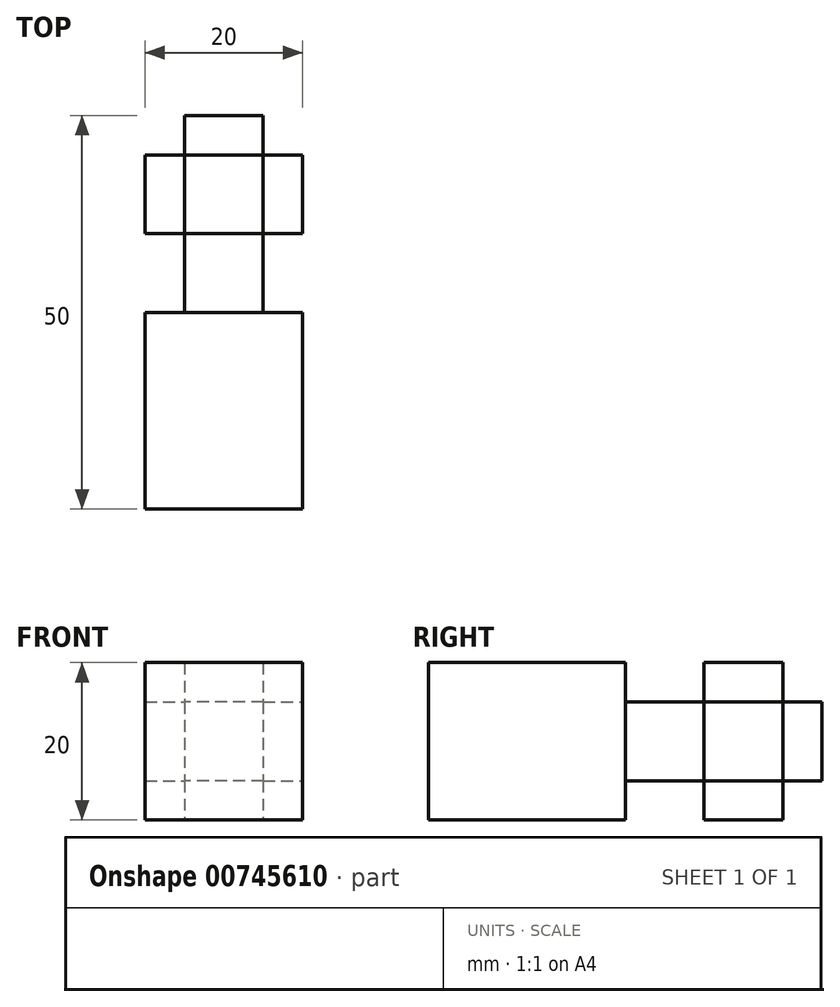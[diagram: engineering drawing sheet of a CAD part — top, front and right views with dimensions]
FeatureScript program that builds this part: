
annotation { "Feature Type Name" : "Feature", "Feature Type Description" : "" }
export const myFeature = defineFeature(function(context is Context, id is Id, definition is map)
    precondition{}
    {
        {
            var Q0;
            Q0=qCreatedBy(makeId("Front.planeOp"),FACE);
            var sketch = newSketch(context, id + "F0", { "sketchPlane" : qUnion([Q0])});
            skLineSegment(sketch, "E0.bottom", {"start": v(-5, 5) * mm, "end": v(5, 5) * mm});
            skLineSegment(sketch, "E0.top", {"start": v(-5, -5) * mm, "end": v(5, -5) * mm});
            skLineSegment(sketch, "E0.left", {"start": v(-5, 5) * mm, "end": v(-5, -5) * mm});
            skLineSegment(sketch, "E0.right", {"start": v(5, 5) * mm, "end": v(5, -5) * mm});
            skPoint(sketch, "E0.middle", {"position": v(0, 0) * mm});
            skSolve(sketch);
        }
        {
            var Q0;
            Q0 = qSketchRegion(id + "F0", true);
            extrude(context, id + "F1", {"entities" : qUnion([Q0]), "depth" : 25 * mm, "offsetDistance" : 25 * mm});
        }
        {
            var Q0;
            Q0=makeQuery(id+"F1.opExtrude","CAP_FACE",FACE,{"disambiguationData":[OSD([sQuery(id+"F0.wireOp",EDGE,"E0.bottom"),sQuery(id+"F0.wireOp",EDGE,"E0.top"),sQuery(id+"F0.wireOp",EDGE,"E0.left"),sQuery(id+"F0.wireOp",EDGE,"E0.right")])],"isStart":false});
            var sketch = newSketch(context, id + "F2", { "sketchPlane" : qUnion([Q0])});
            skLineSegment(sketch, "E1.bottom", {"start": v(-10, 10) * mm, "end": v(10, 10) * mm});
            skLineSegment(sketch, "E1.top", {"start": v(-10, -10) * mm, "end": v(10, -10) * mm});
            skLineSegment(sketch, "E1.left", {"start": v(-10, 10) * mm, "end": v(-10, -10) * mm});
            skLineSegment(sketch, "E1.right", {"start": v(10, 10) * mm, "end": v(10, -10) * mm});
            skPoint(sketch, "E1.middle", {"position": v(0, 0) * mm});
            skSolve(sketch);
        }
        {
            var Q0;
            Q0 = qSketchRegion(id + "F2", true);
            extrude(context, id + "F3", {"entities" : qUnion([Q0]), "operationType" : NewBodyOperationType.ADD, "depth" : 25 * mm, "offsetDistance" : 25 * mm});
        }
        {
            var Q0;
            Q0=makeQuery(id+"F1.opExtrude","SWEPT_FACE",FACE,{"disambiguationData":[OSD([sQuery(id+"F0.wireOp",EDGE,"E0.bottom")])]});
            var sketch = newSketch(context, id + "F4", { "sketchPlane" : qUnion([Q0])});
            skPoint(sketch, "E2", {"position": v(0, -10) * mm});
            skLineSegment(sketch, "E3.bottom", {"start": v(-5, -15) * mm, "end": v(5, -15) * mm});
            skLineSegment(sketch, "E3.top", {"start": v(-5, -5) * mm, "end": v(5, -5) * mm});
            skLineSegment(sketch, "E3.left", {"start": v(-5, -15) * mm, "end": v(-5, -5) * mm});
            skLineSegment(sketch, "E3.right", {"start": v(5, -15) * mm, "end": v(5, -5) * mm});
            skSolve(sketch);
        }
        {
            var Q0;
            Q0 = qSketchRegion(id + "F4", true);
            extrude(context, id + "F5", {"entities" : qUnion([Q0]), "operationType" : NewBodyOperationType.ADD, "depth" : 5 * mm, "offsetDistance" : 25 * mm, "hasSecondDirection" : true, "secondDirectionOppositeDirection" : true, "secondDirectionDepth" : 15 * mm});
        }
        {
            var Q0;
            Q0=makeQuery(id+"F5.boolean.opBoolean","MERGE",FACE,{"derivedFrom":[makeQuery(id+"F1.opExtrude","SWEPT_FACE",FACE,{"disambiguationData":[OSD([sQuery(id+"F0.wireOp",EDGE,"E0.left")])]}),makeQuery(id+"F5.opExtrude","SWEPT_FACE",FACE,{"disambiguationData":[OSD([sQuery(id+"F4.wireOp",EDGE,"E3.left")])]})]});
            var sketch = newSketch(context, id + "F6", { "sketchPlane" : qUnion([Q0])});
            skPoint(sketch, "E4", {"position": v(10, 0) * mm});
            skLineSegment(sketch, "E5.bottom", {"start": v(5, 5) * mm, "end": v(15, 5) * mm});
            skLineSegment(sketch, "E5.top", {"start": v(5, -5) * mm, "end": v(15, -5) * mm});
            skLineSegment(sketch, "E5.left", {"start": v(5, 5) * mm, "end": v(5, -5) * mm});
            skLineSegment(sketch, "E5.right", {"start": v(15, 5) * mm, "end": v(15, -5) * mm});
            skSolve(sketch);
        }
        {
            var Q0;
            Q0 = qSketchRegion(id + "F6", true);
            extrude(context, id + "F7", {"entities" : qUnion([Q0]), "operationType" : NewBodyOperationType.ADD, "depth" : 5 * mm, "offsetDistance" : 25 * mm, "hasSecondDirection" : true, "secondDirectionOppositeDirection" : true, "secondDirectionDepth" : 15 * mm});
        }
    });
